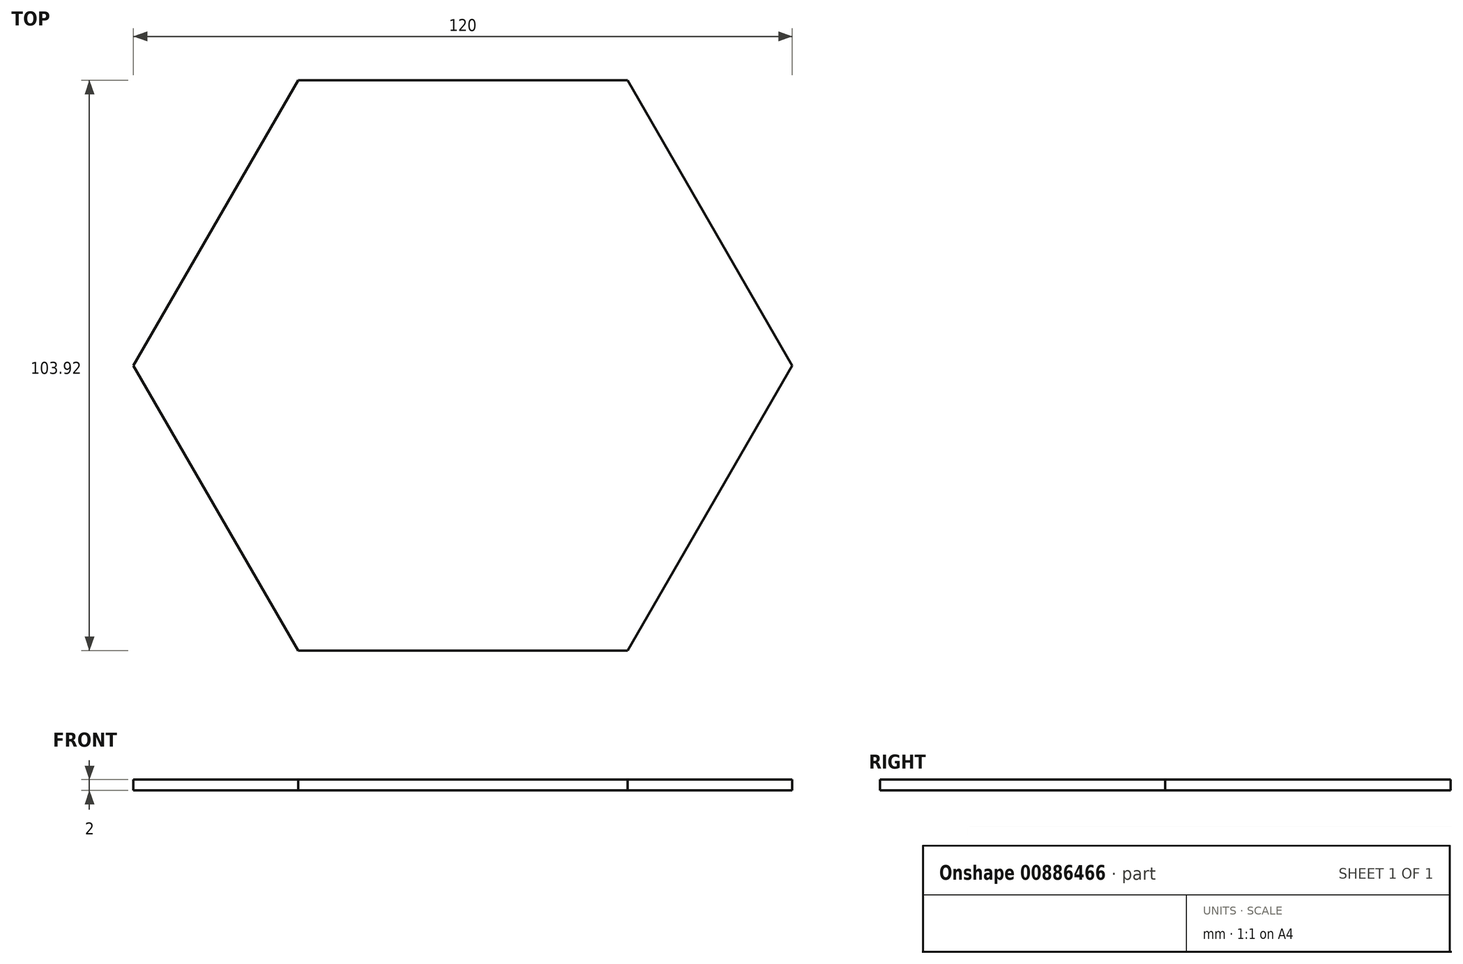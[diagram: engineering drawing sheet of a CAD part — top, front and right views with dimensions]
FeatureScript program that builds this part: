
annotation { "Feature Type Name" : "Feature", "Feature Type Description" : "" }
export const myFeature = defineFeature(function(context is Context, id is Id, definition is map)
    precondition{}
    {
        {
            var Q0;
            Q0=qCreatedBy(makeId("Top.planeOp"),FACE);
            var sketch = newSketch(context, id + "F0", { "sketchPlane" : qUnion([Q0])});
            skCircle(sketch, "E0.cCircle", {"center": v(0, 0) * mm, "radius": 60 * mm, "construction": true});
            skLineSegment(sketch, "E0.0", {"start": v(-60, 0) * mm, "end": v(-30, 51.96) * mm});
            skLineSegment(sketch, "E0.1", {"start": v(-30, 51.96) * mm, "end": v(30, 51.96) * mm});
            skLineSegment(sketch, "E0.2", {"start": v(30, 51.96) * mm, "end": v(60, 0) * mm});
            skLineSegment(sketch, "E0.3", {"start": v(60, 0) * mm, "end": v(30, -51.96) * mm});
            skLineSegment(sketch, "E0.4", {"start": v(30, -51.96) * mm, "end": v(-30, -51.96) * mm});
            skLineSegment(sketch, "E0.5", {"start": v(-30, -51.96) * mm, "end": v(-60, 0) * mm});
            skSolve(sketch);
        }
        {
            var Q0;
            Q0=makeQuery(id+"F0.imprint","IMPRINT",FACE,{"disambiguationData":[TD([[makeQuery(id+"F0.imprint","IMPRINT",EDGE,{"derivedFrom":sQuery(id+"F0.wireOp",EDGE,"E0.0")}),-1.0]])]});
            extrude(context, id + "F1", {"entities" : qUnion([Q0]), "flatOperationType" : FlatOperationType.REMOVE, "depth" : 2 * mm, "offsetDistance" : 25 * mm, "domain" : OperationDomain.MODEL});
        }
    });
